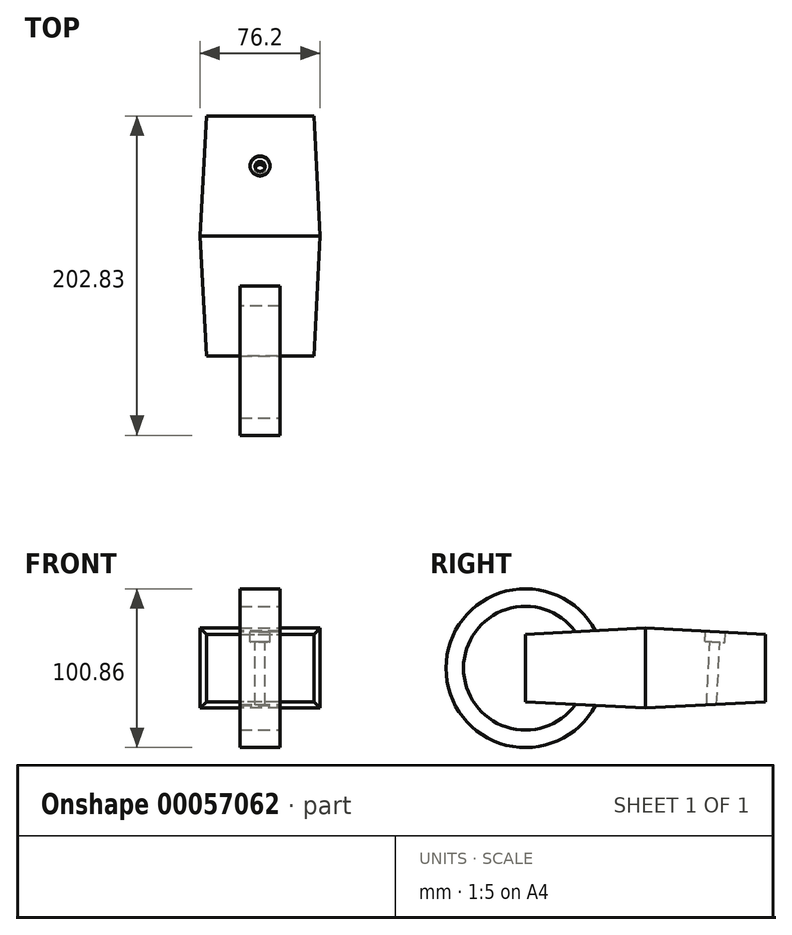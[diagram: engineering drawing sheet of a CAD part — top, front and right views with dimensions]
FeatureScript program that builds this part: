
annotation { "Feature Type Name" : "Feature", "Feature Type Description" : "" }
export const myFeature = defineFeature(function(context is Context, id is Id, definition is map)
    precondition{}
    {
        {
            var Q0;
            Q0=qCreatedBy(makeId("Front.planeOp"),FACE);
            var sketch = newSketch(context, id + "F0", { "sketchPlane" : qUnion([Q0])});
            skLineSegment(sketch, "E0.rect.bottom", {"start": v(-38.1, 25.4) * mm, "end": v(38.1, 25.4) * mm});
            skLineSegment(sketch, "E0.rect.top", {"start": v(-38.1, -25.4) * mm, "end": v(38.1, -25.4) * mm});
            skLineSegment(sketch, "E0.rect.left", {"start": v(-38.1, 25.4) * mm, "end": v(-38.1, -25.4) * mm});
            skLineSegment(sketch, "E0.rect.right", {"start": v(38.1, 25.4) * mm, "end": v(38.1, -25.4) * mm});
            skPoint(sketch, "E0.rect.middle", {"position": v(0, 0) * mm});
            skSolve(sketch);
        }
        {
            var Q0;
            Q0 = qSketchRegion(id + "F0", true);
            extrude(context, id + "F1", {"entities" : qUnion([Q0]), "endBound" : BoundingType.SYMMETRIC, "depth" : 152.4 * mm, "hasDraft" : true, "draftAngle" : 3 * degree, "draftPullDirection" : true});
        }
        {
            var Q0;
            Q0=makeQuery(id+"F1.split0.splitOp","SPLIT",FACE,{"derivedFrom":makeQuery(id+"F1.opExtrude","SWEPT_FACE",FACE,{"disambiguationData":[OSD([sQuery(id+"F0.wireOp",EDGE,"E0.rect.bottom")])]})});
            var sketch = newSketch(context, id + "F2", { "sketchPlane" : qUnion([Q0])});
            skLineSegment(sketch, "E1.rect.bottom", {"start": v(12.7, -43.12) * mm, "end": v(-12.7, -43.12) * mm});
            skLineSegment(sketch, "E1.rect.top", {"start": v(12.7, -30.42) * mm, "end": v(-12.7, -30.42) * mm});
            skLineSegment(sketch, "E1.rect.left", {"start": v(12.7, -43.12) * mm, "end": v(12.7, -30.42) * mm});
            skLineSegment(sketch, "E1.rect.right", {"start": v(-12.7, -43.12) * mm, "end": v(-12.7, -30.42) * mm});
            skPoint(sketch, "E1.rect.middle", {"position": v(0, -36.77) * mm});
            skSolve(sketch);
        }
        {
            var Q0;
            Q0=qCreatedBy(makeId("Right.planeOp"),FACE);
            var sketch = newSketch(context, id + "F3", { "sketchPlane" : qUnion([Q0])});
            skArc(sketch, "E2", {"start": v(-38.05, 23.4) * mm, "mid": v(-119.28, -12.16) * mm, "end": v(-31.44, 0) * mm});
            skPoint(sketch, "E3.0", {"position": v(-38.05, 23.4) * mm});
            skSolve(sketch);
        }
        {
            var Q0;
            Q0 = qSketchRegion(id + "F2", true);
            var Q1;
            Q1 = qConstructionFilter(qBodyType(qCreatedBy(id + "F3" ,EDGE), BodyType.WIRE), ConstructionObject.NO);
            sweep(context, id + "F4", {"operationType" : NewBodyOperationType.ADD, "profiles" : qUnion([Q0]), "path" : qUnion([Q1])});
        }
        {
            var Q0;
            Q0=makeQuery(id+"F1.split0.splitOp","SPLIT",FACE,{"derivedFrom":makeQuery(id+"F1.opExtrude","SWEPT_FACE",FACE,{"disambiguationData":[OSD([sQuery(id+"F0.wireOp",EDGE,"E0.rect.bottom")])]}),"isFromBackBody":true});
            var sketch = newSketch(context, id + "F5", { "sketchPlane" : qUnion([Q0])});
            skPoint(sketch, "E4", {"position": v(0, 43.23) * mm});
            skSolve(sketch);
        }
        {
            var Q0;
            Q0=sQuery(id+"F5.wireOp",VERTEX,"E4");
            var Q1;
            Q1=makeQuery(id+"F1.split0.splitOp","SPLIT",BODY,{"derivedFrom":makeQuery(id+"F1.opExtrude","SWEPT_BODY",BODY,{"disambiguationData":[OSD([sQuery(id+"F0.wireOp",EDGE,"E0.rect.bottom"),sQuery(id+"F0.wireOp",EDGE,"E0.rect.top"),sQuery(id+"F0.wireOp",EDGE,"E0.rect.left"),sQuery(id+"F0.wireOp",EDGE,"E0.rect.right")])]})});
            hole(context, id + "F6", {"style" : HoleStyle.C_BORE, "holeDiameter" : 6.35 * mm, "cBoreDiameter" : 12.7 * mm, "cBoreDepth" : 6.35 * mm, "endStyle" : HoleEndStyle.THROUGH, "locations" : qUnion([Q0]), "scope" : qUnion([Q1])});
        }
    });
